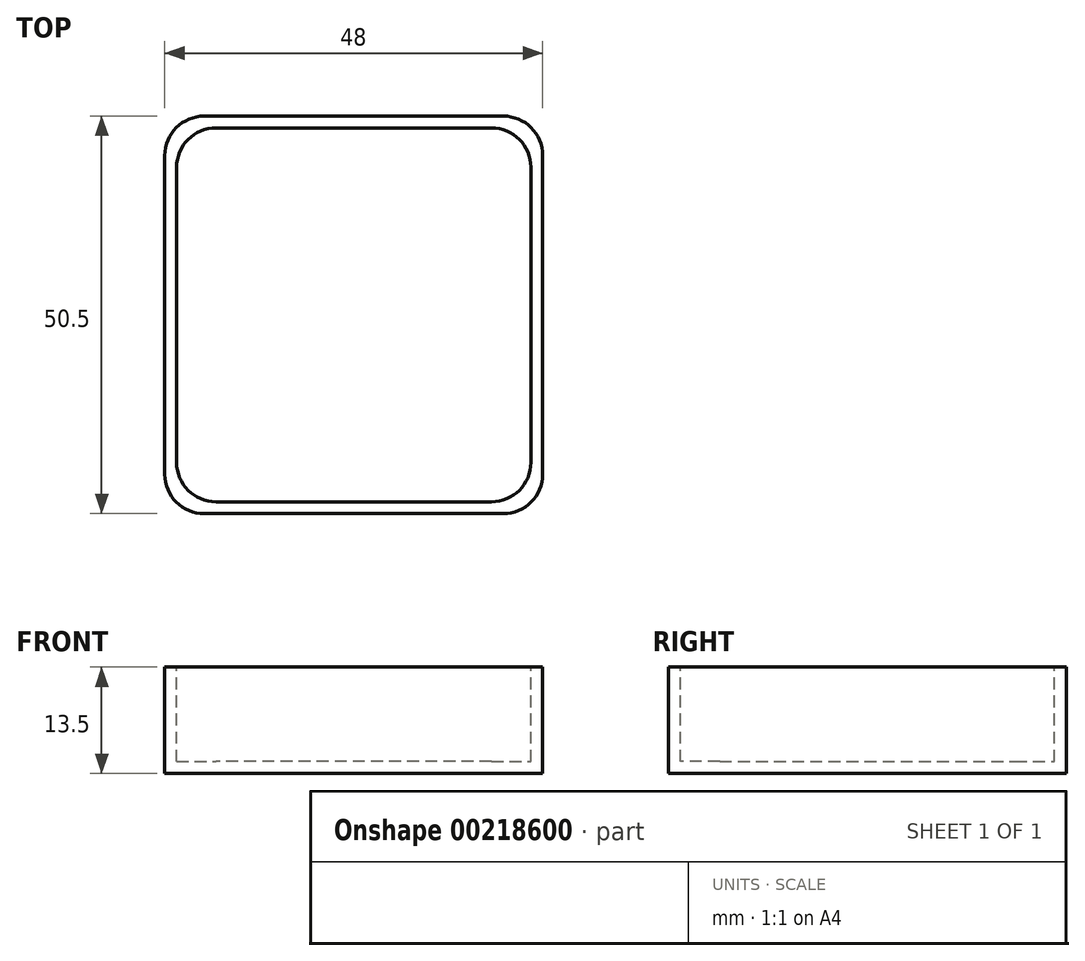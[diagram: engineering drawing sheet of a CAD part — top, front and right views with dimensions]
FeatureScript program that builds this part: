
annotation { "Feature Type Name" : "Feature", "Feature Type Description" : "" }
export const myFeature = defineFeature(function(context is Context, id is Id, definition is map)
    precondition{}
    {
        {
            var Q0;
            Q0=qCreatedBy(makeId("Top.planeOp"),FACE);
            var sketch = newSketch(context, id + "F0", { "sketchPlane" : qUnion([Q0])});
            skLineSegment(sketch, "E0.bottom", {"start": v(-24, -25.25) * mm, "end": v(24, -25.25) * mm});
            skLineSegment(sketch, "E0.top", {"start": v(-24, 25.25) * mm, "end": v(24, 25.25) * mm});
            skLineSegment(sketch, "E0.left", {"start": v(-24, -25.25) * mm, "end": v(-24, 25.25) * mm});
            skLineSegment(sketch, "E0.right", {"start": v(24, -25.25) * mm, "end": v(24, 25.25) * mm});
            skPoint(sketch, "E0.middle", {"position": v(0, 0) * mm});
            skSolve(sketch);
        }
        {
            var Q0;
            Q0 = qSketchRegion(id + "F0", true);
            extrude(context, id + "F1", {"entities" : qUnion([Q0]), "depth" : 13.5 * mm, "offsetDistance" : 25 * mm});
        }
        {
            var Q0;
            Q0=makeQuery(id+"F1.opExtrude","CAP_FACE",FACE,{"disambiguationData":[OSD([sQuery(id+"F0.wireOp",EDGE,"E0.bottom"),sQuery(id+"F0.wireOp",EDGE,"E0.top"),sQuery(id+"F0.wireOp",EDGE,"E0.left"),sQuery(id+"F0.wireOp",EDGE,"E0.right")])],"isStart":false});
            var sketch = newSketch(context, id + "F2", { "sketchPlane" : qUnion([Q0])});
            skLineSegment(sketch, "E1.bottom", {"start": v(22.5, -23.75) * mm, "end": v(-22.5, -23.75) * mm});
            skLineSegment(sketch, "E1.top", {"start": v(22.5, 23.75) * mm, "end": v(-22.5, 23.75) * mm});
            skLineSegment(sketch, "E1.left", {"start": v(22.5, -23.75) * mm, "end": v(22.5, 23.75) * mm});
            skLineSegment(sketch, "E1.right", {"start": v(-22.5, -23.75) * mm, "end": v(-22.5, 23.75) * mm});
            skPoint(sketch, "E1.middle", {"position": v(0, 0) * mm});
            skSolve(sketch);
        }
        {
            var Q0;
            Q0 = qSketchRegion(id + "F2", true);
            extrude(context, id + "F3", {"entities" : qUnion([Q0]), "operationType" : NewBodyOperationType.REMOVE, "oppositeDirection" : true, "depth" : 12 * mm, "offsetDistance" : 25 * mm});
        }
        {
            var Q0;
            Q0=makeQuery(id+"F3.boolean.opBoolean","COPY",EDGE,{"derivedFrom":makeQuery(id+"F3.opExtrude","SWEPT_EDGE",EDGE,{"disambiguationData":[OSD([sQuery(id+"F2.wireOp",EDGE,"E1.top"),sQuery(id+"F2.wireOp",EDGE,"E1.left")])]})});
            var Q1;
            Q1=makeQuery(id+"F3.boolean.opBoolean","COPY",EDGE,{"derivedFrom":makeQuery(id+"F3.opExtrude","SWEPT_EDGE",EDGE,{"disambiguationData":[OSD([sQuery(id+"F2.wireOp",EDGE,"E1.top"),sQuery(id+"F2.wireOp",EDGE,"E1.right")])]})});
            var Q2;
            Q2=makeQuery(id+"F3.boolean.opBoolean","COPY",EDGE,{"derivedFrom":makeQuery(id+"F3.opExtrude","SWEPT_EDGE",EDGE,{"disambiguationData":[OSD([sQuery(id+"F2.wireOp",EDGE,"E1.bottom"),sQuery(id+"F2.wireOp",EDGE,"E1.left")])]})});
            var Q3;
            Q3=makeQuery(id+"F3.boolean.opBoolean","COPY",EDGE,{"derivedFrom":makeQuery(id+"F3.opExtrude","SWEPT_EDGE",EDGE,{"disambiguationData":[OSD([sQuery(id+"F2.wireOp",EDGE,"E1.bottom"),sQuery(id+"F2.wireOp",EDGE,"E1.right")])]})});
            var Q4;
            Q4=makeQuery(id+"F1.opExtrude","SWEPT_EDGE",EDGE,{"disambiguationData":[OSD([sQuery(id+"F0.wireOp",EDGE,"E0.bottom"),sQuery(id+"F0.wireOp",EDGE,"E0.left")])]});
            var Q5;
            Q5=makeQuery(id+"F1.opExtrude","SWEPT_EDGE",EDGE,{"disambiguationData":[OSD([sQuery(id+"F0.wireOp",EDGE,"E0.bottom"),sQuery(id+"F0.wireOp",EDGE,"E0.right")])]});
            var Q6;
            Q6=makeQuery(id+"F1.opExtrude","SWEPT_EDGE",EDGE,{"disambiguationData":[OSD([sQuery(id+"F0.wireOp",EDGE,"E0.top"),sQuery(id+"F0.wireOp",EDGE,"E0.left")])]});
            var Q7;
            Q7=makeQuery(id+"F1.opExtrude","SWEPT_EDGE",EDGE,{"disambiguationData":[OSD([sQuery(id+"F0.wireOp",EDGE,"E0.top"),sQuery(id+"F0.wireOp",EDGE,"E0.right")])]});
            fillet(context, id + "F4", {"entities" : qUnion([Q0, Q1, Q2, Q3, Q4, Q5, Q6, Q7]), "radius" : 5 * mm, "tangentPropagation" : true, "allowEdgeOverflow" : false});
        }
    });
